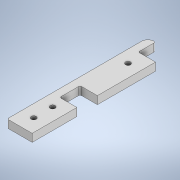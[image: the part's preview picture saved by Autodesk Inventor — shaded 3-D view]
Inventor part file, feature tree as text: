
AUTODESK INVENTOR PART (.ipt)
format: ipt  version: 2021 (Build 250183000, 183)  size: 137,728 bytes
history: native  units: mm
features: sketch x2, extrude x1, hole x1
ambient origin geometry x8: Origin, YZ Plane, XZ Plane, XY Plane, X Axis, Y Axis, Z Axis, Center Point
bodies: Solid1 (feature_tree)
feature tree (4):
  extrude  "Extrusion1"  Depth=15.9mm
  hole  "Hole1"  [1 undecoded]
  sketch  "Sketch1"  dims[d0=15.9mm d1=104.5mm]
  sketch  "Sketch2"  dims[d2=11.0mm d3=11.0mm d4=11.0mm d5=13.0mm d6=56.5mm d7=15.0mm d8=4.0mm d9=1.0mm d10=5.0mm d11=0.0mm d12=8.0mm d13=36.0mm d14=84.0mm d15=3.2mm d16=6.0mm d17=4.0mm d18=2.0mm d19=90.0deg d20=8.0mm d21=20.594885mm d22=1.0mm d23=24.0mm]
note: 1 required parameter value undecoded (feature->parameter linkage not recoverable at this tier; creation-order binding heuristic only, values carry confidence <= 0.55)
